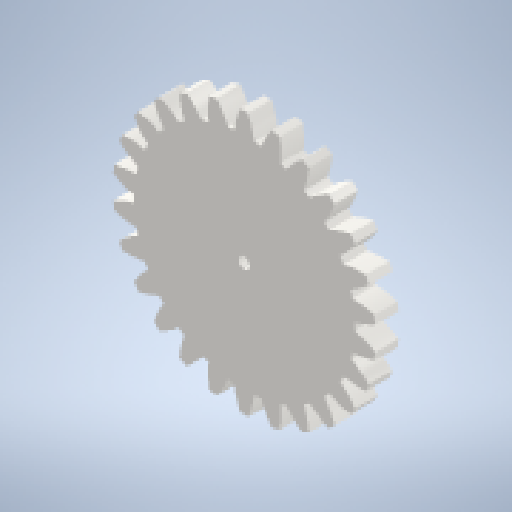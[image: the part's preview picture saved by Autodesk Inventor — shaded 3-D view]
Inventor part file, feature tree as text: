
AUTODESK INVENTOR PART (.ipt)
format: ipt  version: 2024 (Build 280153000, 153)  size: 272,384 bytes
history: native  units: mm (DEFAULTED — no unit token found)
features: plane x3, other x3, extrude x2, sketch x2
ambient origin geometry x8: Origin, YZ Plane, XZ Plane, XY Plane, X Axis, Y Axis, Z Axis, Center Point
bodies: Solid1 (feature_tree)
feature tree (10):
  extrude  "Extrusion1"  Depth=20.0mm TaperAngle=0.0deg
  plane  "Work Plane2"
  plane  "Work Plane8"
  plane  "Work Plane9"
  other  "Spur Gear"
  extrude  "Extrusion2"  Depth=10.0mm TaperAngle=0.0deg
  sketch  "Sketch1"  dims[d0=56.0mm d1=20.0mm d2=0.0mm]
  other  "Srf1"
  sketch  "Sketch3"  dims[d3=52.0mm d4=10.0mm d5=0.0mm d16=36.0mm d17=0.0mm d34=1.208305mm d39=0.0mm d41=0.0mm d43=36.0mm d46=36.0mm d47=0.0mm d48=0.0mm d49=2.5mm d50=10.0mm d51=0.0mm]
  other  "Pitch Diameter"
